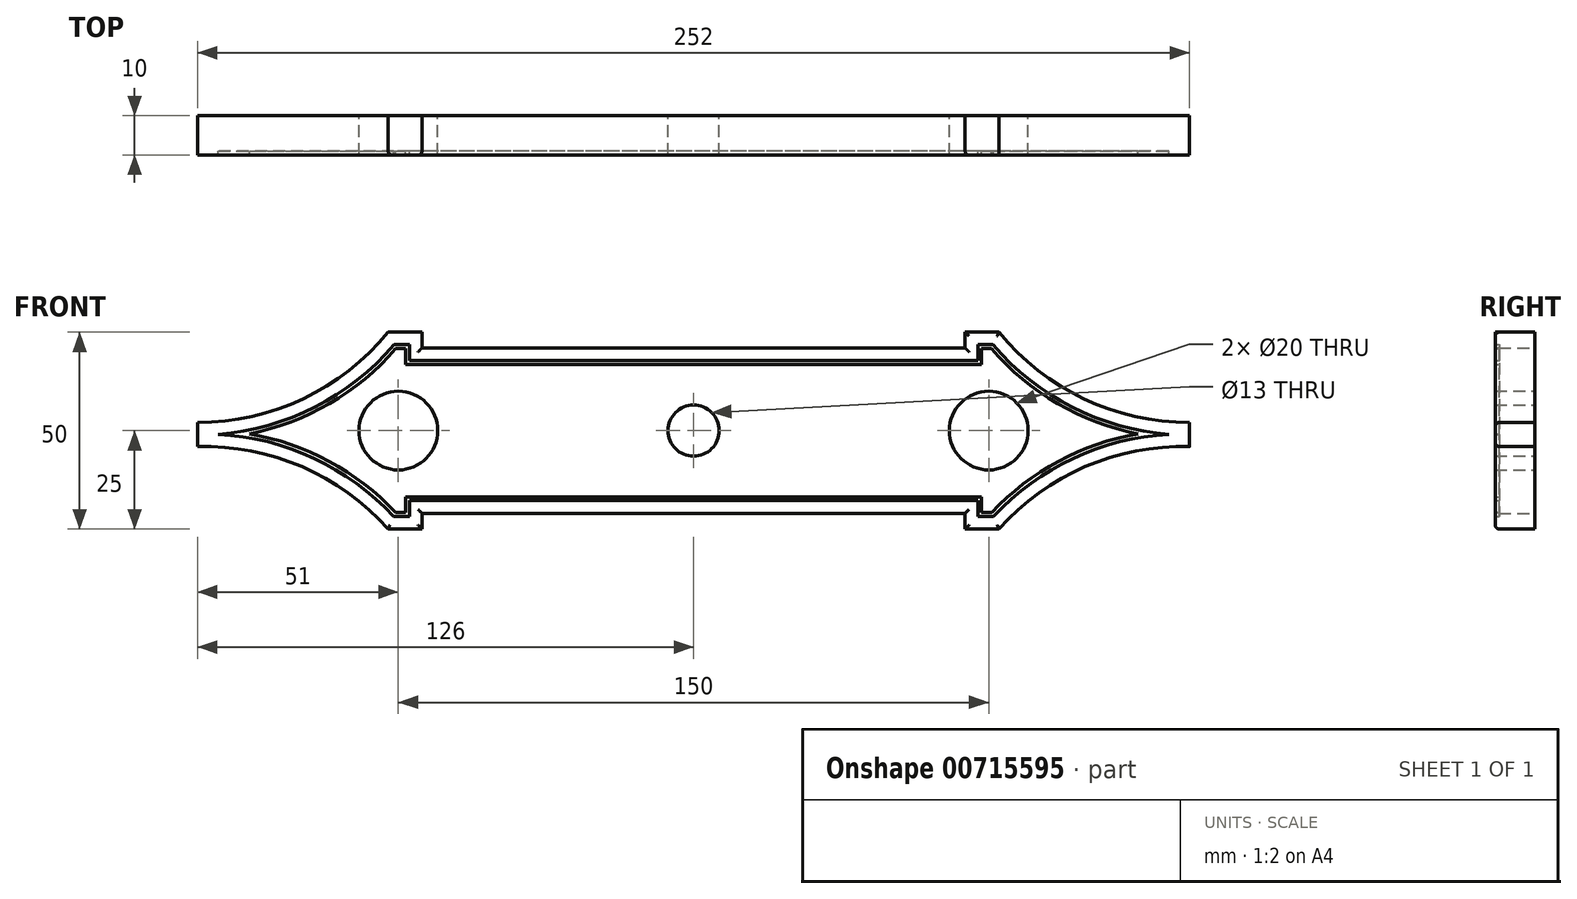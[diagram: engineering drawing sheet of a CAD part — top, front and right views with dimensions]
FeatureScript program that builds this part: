
annotation { "Feature Type Name" : "Feature", "Feature Type Description" : "" }
export const myFeature = defineFeature(function(context is Context, id is Id, definition is map)
    precondition{}
    {
        {
            var Q0;
            Q0=qCreatedBy(makeId("Front.planeOp"),FACE);
            var sketch = newSketch(context, id + "F0", { "sketchPlane" : qUnion([Q0])});
            skLineSegment(sketch, "E0.bottom", {"start": v(77.6, -25) * mm, "end": v(69, -25) * mm});
            skLineSegment(sketch, "E0.top", {"start": v(77.6, 25) * mm, "end": v(69, 25) * mm});
            skLineSegment(sketch, "E0.left", {"start": v(126, -4.06) * mm, "end": v(126, 2.04) * mm});
            skLineSegment(sketch, "E0.right", {"start": v(-126, -4.06) * mm, "end": v(-126, 2.04) * mm});
            skPoint(sketch, "E0.middle", {"position": v(0, 0) * mm});
            skCircle(sketch, "E1", {"center": v(-75, 0) * mm, "radius": 10 * mm});
            skCircle(sketch, "E2", {"center": v(0, 0) * mm, "radius": 6.5 * mm});
            skCircle(sketch, "E3", {"center": v(75, 0) * mm, "radius": 10 * mm});
            skLineSegment(sketch, "E4", {"start": v(-126, 2.04) * mm, "end": v(-126, -4.06) * mm});
            skLineSegment(sketch, "E5", {"start": v(-77.6, 25) * mm, "end": v(-69, 25) * mm});
            skLineSegment(sketch, "E6", {"start": v(-69, -25) * mm, "end": v(-77.6, -25) * mm});
            skArc(sketch, "E7", {"start": v(-126, 2.04) * mm, "mid": v(-99.22, 8.07) * mm, "end": v(-77.6, 25) * mm});
            skArc(sketch, "E8", {"start": v(-77.6, -25) * mm, "mid": v(-99.48, -9.17) * mm, "end": v(-126, -4.06) * mm});
            skLineSegment(sketch, "E9", {"start": v(-69, -25) * mm, "end": v(-69, -21) * mm});
            skLineSegment(sketch, "E10", {"start": v(-69, 25) * mm, "end": v(-69, 21) * mm});
            skPoint(sketch, "E11.orphan", {"position": v(-126, 25) * mm});
            skPoint(sketch, "E12.orphan", {"position": v(-126, -25) * mm});
            skLineSegment(sketch, "E13", {"start": v(126, 2.04) * mm, "end": v(126, -4.06) * mm});
            skArc(sketch, "E14", {"start": v(77.6, 25) * mm, "mid": v(99.22, 8.07) * mm, "end": v(126, 2.04) * mm});
            skArc(sketch, "E15", {"start": v(126, -4.06) * mm, "mid": v(99.48, -9.17) * mm, "end": v(77.6, -25) * mm});
            skPoint(sketch, "E16.orphan", {"position": v(126, 25) * mm});
            skPoint(sketch, "E17.orphan", {"position": v(126, -25) * mm});
            skLineSegment(sketch, "E18", {"start": v(69, 25) * mm, "end": v(69, 21) * mm});
            skLineSegment(sketch, "E19", {"start": v(69, -25) * mm, "end": v(69, -21) * mm});
            skLineSegment(sketch, "E20", {"start": v(69, -21) * mm, "end": v(-69, -21) * mm});
            skLineSegment(sketch, "E21", {"start": v(-69, 21) * mm, "end": v(69, 21) * mm});
            skLineSegment(sketch, "E22.trimOffspring", {"start": v(-69, 25) * mm, "end": v(-77.6, 25) * mm});
            skLineSegment(sketch, "E23.0", {"start": v(-72.19, 21.8) * mm, "end": v(-72.19, 17.8) * mm});
            skLineSegment(sketch, "E23.1", {"start": v(-72.19, 21.8) * mm, "end": v(-76.1, 21.8) * mm});
            skArc(sketch, "E23.2", {"start": v(-120.77, -0.94) * mm, "mid": v(-96.19, 6) * mm, "end": v(-76.1, 21.8) * mm});
            skArc(sketch, "E23.3", {"start": v(120.77, -0.94) * mm, "mid": v(96.45, -7.04) * mm, "end": v(76.19, -21.8) * mm});
            skArc(sketch, "E23.4", {"start": v(76.1, 21.81) * mm, "mid": v(96.19, 6) * mm, "end": v(120.77, -0.94) * mm});
            skLineSegment(sketch, "E23.5", {"start": v(76.1, 21.81) * mm, "end": v(72.19, 21.81) * mm});
            skLineSegment(sketch, "E23.6", {"start": v(72.19, 21.81) * mm, "end": v(72.19, 17.81) * mm});
            skLineSegment(sketch, "E23.7", {"start": v(76.19, -21.8) * mm, "end": v(72.2, -21.8) * mm});
            skLineSegment(sketch, "E23.8", {"start": v(72.2, -21.8) * mm, "end": v(72.2, -17.8) * mm});
            skLineSegment(sketch, "E23.9", {"start": v(72.19, -17.8) * mm, "end": v(-72.19, -17.81) * mm});
            skLineSegment(sketch, "E23.10", {"start": v(-72.19, 17.8) * mm, "end": v(72.19, 17.81) * mm});
            skLineSegment(sketch, "E23.11", {"start": v(-72.19, -21.81) * mm, "end": v(-72.19, -17.81) * mm});
            skLineSegment(sketch, "E23.12", {"start": v(-72.19, -21.81) * mm, "end": v(-76.19, -21.81) * mm});
            skArc(sketch, "E23.13", {"start": v(-76.19, -21.81) * mm, "mid": v(-96.45, -7.04) * mm, "end": v(-120.77, -0.94) * mm});
            skLineSegment(sketch, "E24.0", {"start": v(-73.19, 20.8) * mm, "end": v(-73.19, 16.8) * mm});
            skArc(sketch, "E24.1", {"start": v(-112.84, -0.84) * mm, "mid": v(-92.45, 6.9) * mm, "end": v(-75.65, 20.8) * mm});
            skLineSegment(sketch, "E24.2", {"start": v(-73.19, 16.8) * mm, "end": v(73.2, 16.81) * mm});
            skLineSegment(sketch, "E24.5", {"start": v(73.2, -16.8) * mm, "end": v(-73.19, -16.81) * mm});
            skLineSegment(sketch, "E24.6", {"start": v(73.2, 20.81) * mm, "end": v(73.2, 16.81) * mm});
            skArc(sketch, "E24.7", {"start": v(75.65, 20.8) * mm, "mid": v(92.45, 6.9) * mm, "end": v(112.84, -0.84) * mm});
            skArc(sketch, "E24.8", {"start": v(112.84, -0.84) * mm, "mid": v(92.68, -7.82) * mm, "end": v(75.76, -20.8) * mm});
            skLineSegment(sketch, "E24.9", {"start": v(73.2, -20.8) * mm, "end": v(73.2, -16.8) * mm});
            skLineSegment(sketch, "E25", {"start": v(-75.65, -20.81) * mm, "end": v(-73.19, -20.81) * mm});
            skLineSegment(sketch, "E26.trimOffspring", {"start": v(-73.19, -20.81) * mm, "end": v(-73.19, -16.81) * mm});
            skLineSegment(sketch, "E27", {"start": v(-75.65, 20.8) * mm, "end": v(-73.19, 20.8) * mm});
            skArc(sketch, "E28", {"start": v(-75.65, -20.8) * mm, "mid": v(-92.63, -7.8) * mm, "end": v(-112.84, -0.84) * mm});
            skLineSegment(sketch, "E29", {"start": v(73.2, 20.81) * mm, "end": v(75.65, 20.81) * mm});
            skLineSegment(sketch, "E30", {"start": v(73.2, -20.8) * mm, "end": v(75.76, -20.8) * mm});
            skSolve(sketch);
        }
        {
            var Q0;
            Q0 = qSketchRegion(id + "F0", true);
            var Q1;
            Q1=makeQuery(id+"F0.imprint","IMPRINT",FACE,{"disambiguationData":[TD([[makeQuery(id+"F0.imprint","IMPRINT",EDGE,{"derivedFrom":sQuery(id+"F0.wireOp",EDGE,"E1")}),-1.0]])]});
            extrude(context, id + "F1", {"entities" : qUnion([Q0, Q1]), "depth" : 10 * mm, "offsetDistance" : 25 * mm});
        }
        {
            var Q0;
            Q0=makeQuery(id+"F0.imprint","IMPRINT",FACE,{"disambiguationData":[TD([[makeQuery(id+"F0.imprint","IMPRINT",EDGE,{"derivedFrom":sQuery(id+"F0.wireOp",EDGE,"E23.0")}),-1.0]])]});
            extrude(context, id + "F2", {"entities" : qUnion([Q0]), "operationType" : NewBodyOperationType.ADD, "depth" : 9 * mm, "offsetDistance" : 25 * mm});
        }
        {
            var Q0;
            Q0=makeQuery(id+"F1.opExtrude","CAP_EDGE",EDGE,{"disambiguationData":[OSD([sQuery(id+"F0.wireOp",EDGE,"E7")])],"isStart":false});
            var Q1;
            Q1=makeQuery(id+"F1.opExtrude","CAP_EDGE",EDGE,{"disambiguationData":[OSD([sQuery(id+"F0.wireOp",EDGE,"E4")])],"isStart":false});
            var Q2;
            Q2=makeQuery(id+"F1.opExtrude","CAP_EDGE",EDGE,{"disambiguationData":[OSD([sQuery(id+"F0.wireOp",EDGE,"E8")])],"isStart":false});
            var Q3;
            Q3=makeQuery(id+"F1.opExtrude","CAP_EDGE",EDGE,{"disambiguationData":[OSD([sQuery(id+"F0.wireOp",EDGE,"E6")])],"isStart":false});
            var Q4;
            Q4=makeQuery(id+"F1.opExtrude","CAP_EDGE",EDGE,{"disambiguationData":[OSD([sQuery(id+"F0.wireOp",EDGE,"E9")])],"isStart":false});
            var Q5;
            Q5=makeQuery(id+"F1.opExtrude","CAP_EDGE",EDGE,{"disambiguationData":[OSD([sQuery(id+"F0.wireOp",EDGE,"E20")])],"isStart":false});
            var Q6;
            Q6=makeQuery(id+"F1.opExtrude","CAP_EDGE",EDGE,{"disambiguationData":[OSD([sQuery(id+"F0.wireOp",EDGE,"E22.trimOffspring")])],"isStart":false});
            var Q7;
            Q7=makeQuery(id+"F1.opExtrude","CAP_EDGE",EDGE,{"disambiguationData":[OSD([sQuery(id+"F0.wireOp",EDGE,"E10")])],"isStart":false});
            var Q8;
            Q8=makeQuery(id+"F1.opExtrude","CAP_EDGE",EDGE,{"disambiguationData":[OSD([sQuery(id+"F0.wireOp",EDGE,"E21")])],"isStart":false});
            var Q9;
            Q9=makeQuery(id+"F1.opExtrude","CAP_EDGE",EDGE,{"disambiguationData":[OSD([sQuery(id+"F0.wireOp",EDGE,"E19")])],"isStart":false});
            var Q10;
            Q10=makeQuery(id+"F1.opExtrude","CAP_EDGE",EDGE,{"disambiguationData":[OSD([sQuery(id+"F0.wireOp",EDGE,"E0.bottom")])],"isStart":false});
            var Q11;
            Q11=makeQuery(id+"F1.opExtrude","CAP_EDGE",EDGE,{"disambiguationData":[OSD([sQuery(id+"F0.wireOp",EDGE,"E15")])],"isStart":false});
            var Q12;
            Q12=makeQuery(id+"F1.opExtrude","CAP_EDGE",EDGE,{"disambiguationData":[OSD([sQuery(id+"F0.wireOp",EDGE,"E13")])],"isStart":false});
            var Q13;
            Q13=makeQuery(id+"F1.opExtrude","CAP_EDGE",EDGE,{"disambiguationData":[OSD([sQuery(id+"F0.wireOp",EDGE,"E14")])],"isStart":false});
            var Q14;
            Q14=makeQuery(id+"F1.opExtrude","CAP_EDGE",EDGE,{"disambiguationData":[OSD([sQuery(id+"F0.wireOp",EDGE,"E0.top")])],"isStart":false});
            var Q15;
            Q15=makeQuery(id+"F1.opExtrude","CAP_EDGE",EDGE,{"disambiguationData":[OSD([sQuery(id+"F0.wireOp",EDGE,"E18")])],"isStart":false});
            fillet(context, id + "F3", {"entities" : qUnion([Q0, Q1, Q2, Q3, Q4, Q5, Q6, Q7, Q8, Q9, Q10, Q11, Q12, Q13, Q14, Q15]), "radius" : 1 * mm, "tangentPropagation" : true, "allowEdgeOverflow" : false});
        }
    });
